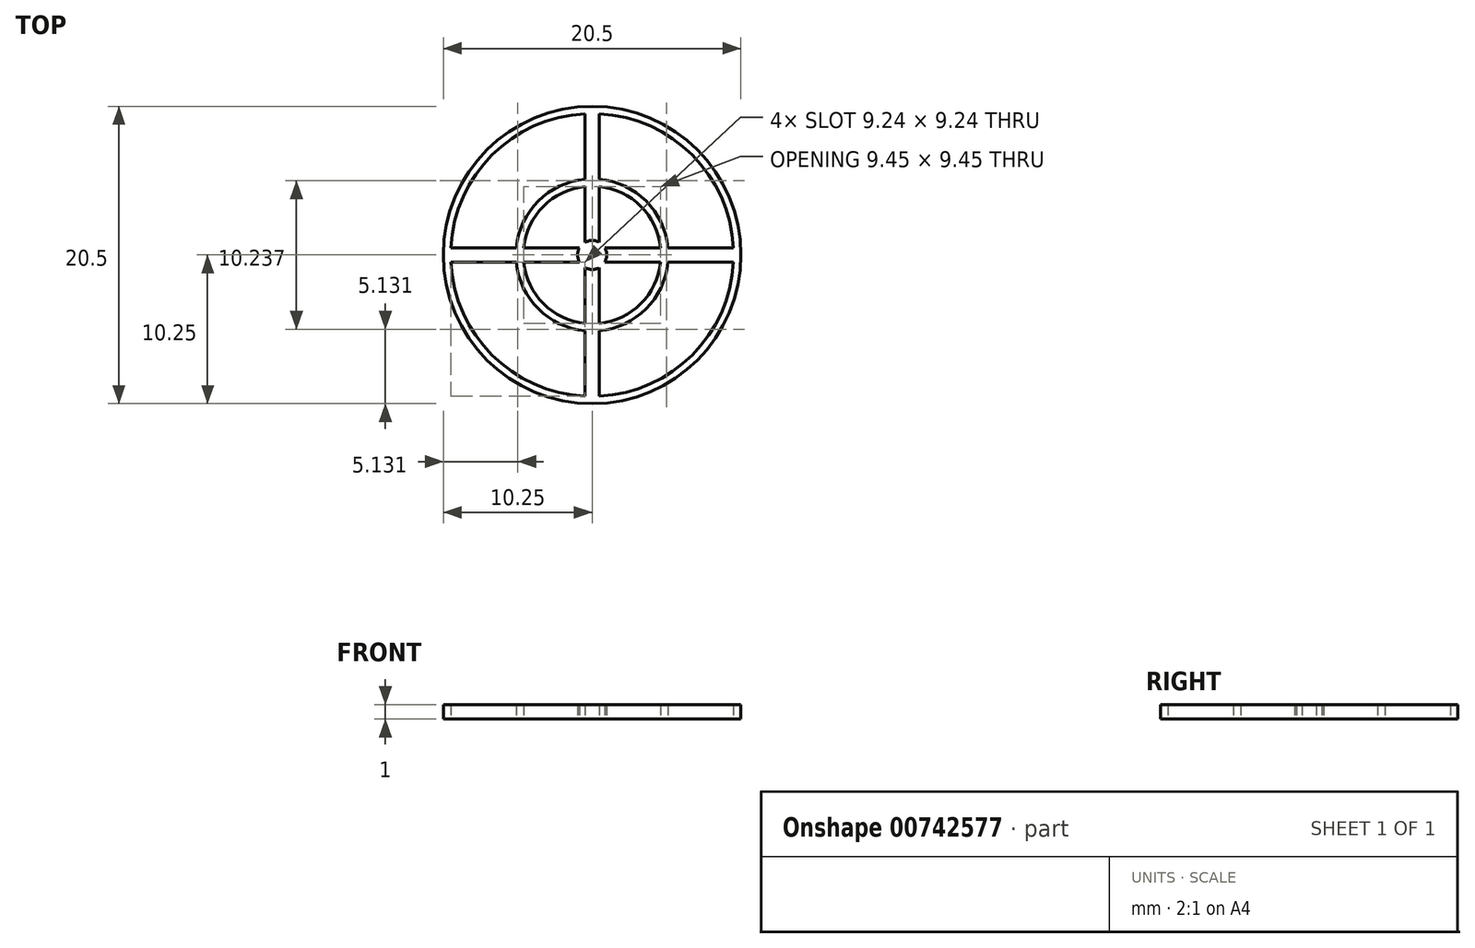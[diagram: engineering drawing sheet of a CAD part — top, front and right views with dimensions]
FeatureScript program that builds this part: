
annotation { "Feature Type Name" : "Feature", "Feature Type Description" : "" }
export const myFeature = defineFeature(function(context is Context, id is Id, definition is map)
    precondition{}
    {
        {
            var Q0;
            Q0=qCreatedBy(makeId("Top.planeOp"),FACE);
            var sketch = newSketch(context, id + "F0", { "sketchPlane" : qUnion([Q0])});
            skLineSegment(sketch, "E0.bottom", {"start": v(-10, 0.5) * mm, "end": v(10, 0.5) * mm});
            skLineSegment(sketch, "E0.top", {"start": v(-10, -0.5) * mm, "end": v(10, -0.5) * mm});
            skLineSegment(sketch, "E0.left", {"start": v(-10, 0.5) * mm, "end": v(-10, -0.5) * mm});
            skLineSegment(sketch, "E0.right", {"start": v(10, 0.5) * mm, "end": v(10, -0.5) * mm});
            skPoint(sketch, "E0.middle", {"position": v(0, 0) * mm});
            skLineSegment(sketch, "E1.bottom", {"start": v(-0.5, 10) * mm, "end": v(0.5, 10) * mm});
            skLineSegment(sketch, "E1.top", {"start": v(-0.5, -10) * mm, "end": v(0.5, -10) * mm});
            skLineSegment(sketch, "E1.left", {"start": v(-0.5, 10) * mm, "end": v(-0.5, -10) * mm});
            skLineSegment(sketch, "E1.right", {"start": v(0.5, 10) * mm, "end": v(0.5, -10) * mm});
            skSolve(sketch);
        }
        {
            var Q0;
            Q0 = qSketchRegion(id + "F0", true);
            extrude(context, id + "F1", {"entities" : qUnion([Q0]), "depth" : 1 * mm, "offsetDistance" : 25 * mm});
        }
        {
            var Q0;
            Q0=qCreatedBy(makeId("Top.planeOp"),FACE);
            var sketch = newSketch(context, id + "F2", { "sketchPlane" : qUnion([Q0])});
            skCircle(sketch, "E2", {"center": v(0, 0) * mm, "radius": 4.75 * mm});
            skCircle(sketch, "E3", {"center": v(0, 0) * mm, "radius": 5.25 * mm});
            skCircle(sketch, "E4", {"center": v(0, 0) * mm, "radius": 10.25 * mm});
            skCircle(sketch, "E5", {"center": v(0, 0) * mm, "radius": 9.75 * mm});
            skSolve(sketch);
        }
        {
            var Q0;
            Q0 = qSketchRegion(id + "F2", true);
            var Q1;
            Q1=makeQuery(id+"F2.imprint","IMPRINT",FACE,{"disambiguationData":[TD([[makeQuery(id+"F2.imprint","IMPRINT",EDGE,{"derivedFrom":sQuery(id+"F2.wireOp",EDGE,"E2")}),-1.0]])]});
            extrude(context, id + "F3", {"entities" : qUnion([Q0, Q1]), "operationType" : NewBodyOperationType.ADD, "depth" : 1 * mm, "offsetDistance" : 25 * mm});
        }
        {
            var Q0;
            Q0=qCreatedBy(makeId("Top.planeOp"),FACE);
            var sketch = newSketch(context, id + "F4", { "sketchPlane" : qUnion([Q0])});
            skCircle(sketch, "E6", {"center": v(0, 0) * mm, "radius": 1 * mm});
            skSolve(sketch);
        }
        {
            var Q0;
            Q0 = qSketchRegion(id + "F4", true);
            extrude(context, id + "F5", {"entities" : qUnion([Q0]), "operationType" : NewBodyOperationType.REMOVE, "depth" : 25 * mm, "offsetDistance" : 25 * mm});
        }
    });
